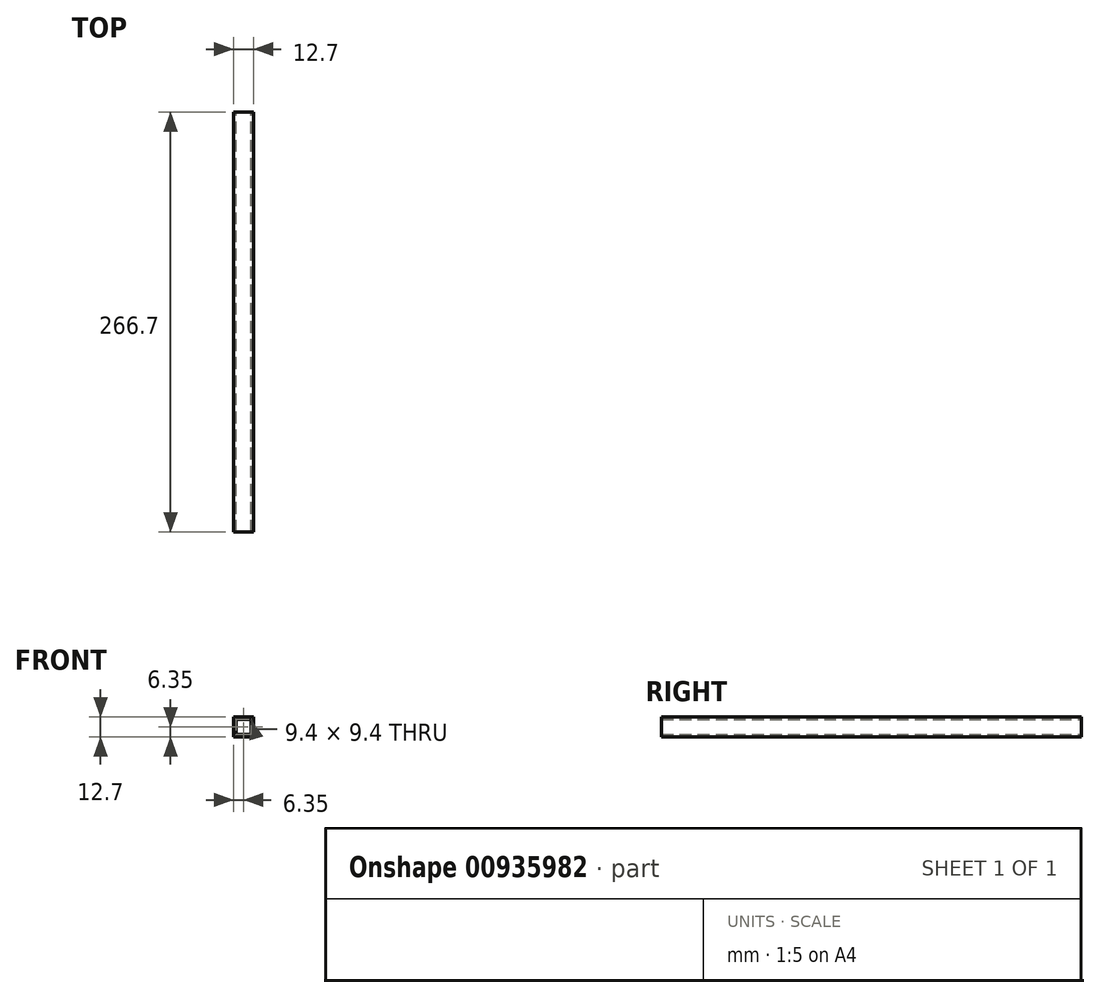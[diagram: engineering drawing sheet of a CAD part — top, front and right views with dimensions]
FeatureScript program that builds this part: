
annotation { "Feature Type Name" : "Feature", "Feature Type Description" : "" }
export const myFeature = defineFeature(function(context is Context, id is Id, definition is map)
    precondition{}
    {
        {
            var Q0;
            Q0=qCreatedBy(makeId("Front.planeOp"),FACE);
            var sketch = newSketch(context, id + "F0", { "sketchPlane" : qUnion([Q0])});
            skLineSegment(sketch, "E0.bottom", {"start": v(6.35, -6.35) * mm, "end": v(-6.35, -6.35) * mm});
            skLineSegment(sketch, "E0.top", {"start": v(6.35, 6.35) * mm, "end": v(-6.35, 6.35) * mm});
            skLineSegment(sketch, "E0.left", {"start": v(6.35, -6.35) * mm, "end": v(6.35, 6.35) * mm});
            skLineSegment(sketch, "E0.right", {"start": v(-6.35, -6.35) * mm, "end": v(-6.35, 6.35) * mm});
            skPoint(sketch, "E0.middle", {"position": v(0, 0) * mm});
            skLineSegment(sketch, "E1.bottom", {"start": v(4.7, -4.7) * mm, "end": v(-4.7, -4.7) * mm});
            skLineSegment(sketch, "E1.top", {"start": v(4.7, 4.7) * mm, "end": v(-4.7, 4.7) * mm});
            skLineSegment(sketch, "E1.left", {"start": v(4.7, -4.7) * mm, "end": v(4.7, 4.7) * mm});
            skLineSegment(sketch, "E1.right", {"start": v(-4.7, -4.7) * mm, "end": v(-4.7, 4.7) * mm});
            skSolve(sketch);
        }
        {
            var Q0;
            Q0 = qSketchRegion(id + "F0", true);
            extrude(context, id + "F1", {"entities" : qUnion([Q0]), "depth" : 266.7 * mm, "offsetDistance" : 25.4 * mm});
        }
    });
